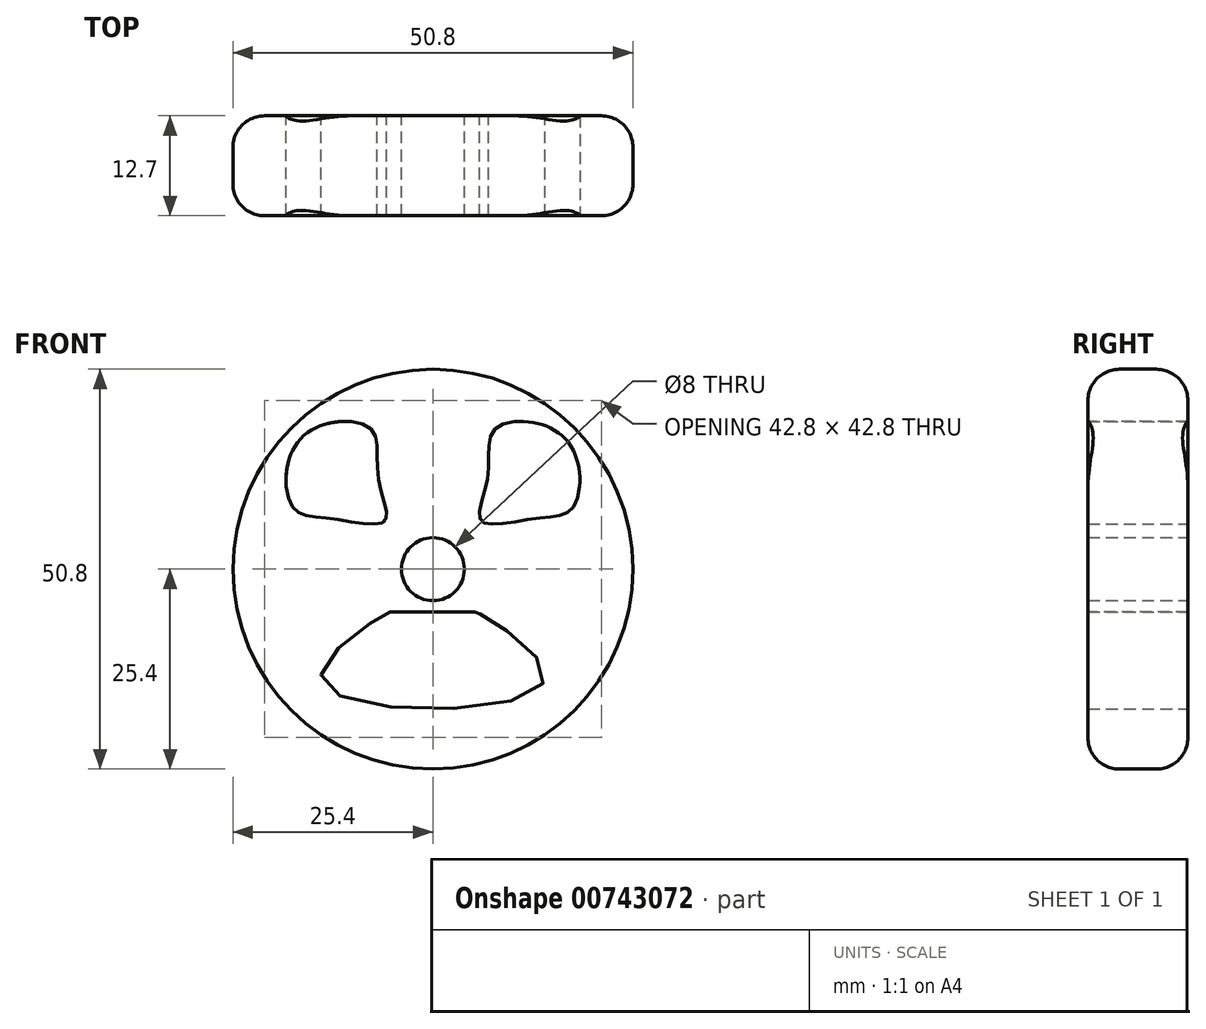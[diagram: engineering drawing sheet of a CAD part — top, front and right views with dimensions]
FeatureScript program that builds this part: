
annotation { "Feature Type Name" : "Feature", "Feature Type Description" : "" }
export const myFeature = defineFeature(function(context is Context, id is Id, definition is map)
    precondition{}
    {
        {
            var Q0;
            Q0=qCreatedBy(makeId("Front.planeOp"),FACE);
            var sketch = newSketch(context, id + "F0", { "sketchPlane" : qUnion([Q0])});
            skCircle(sketch, "E0", {"center": v(0, 0) * mm, "radius": 25.4 * mm});
            skCircle(sketch, "E1", {"center": v(0, 0) * mm, "radius": 4 * mm});
            skLineSegment(sketch, "E2", {"start": v(-17.96, 17.96) * mm, "end": v(0, 0) * mm, "construction": true});
            skLineSegment(sketch, "E3.MirrorCS", {"start": v(17.96, 17.96) * mm, "end": v(0, 0) * mm, "construction": true});
            skLineSegment(sketch, "E4", {"start": v(-14.15, -14.15) * mm, "end": v(14.15, -14.15) * mm, "construction": true});
            skLineSegment(sketch, "E5", {"start": v(-5.44, -5.44) * mm, "end": v(5.44, -5.44) * mm, "construction": true});
            skFitSpline(sketch, "E6", {"points": [v(-5.44, -5.44) * mm, v(-5.37, -5.44) * mm, v(-5.33, -5.44) * mm, v(-5.25, -5.44) * mm, v(-5.07, -5.44) * mm, v(-4.94, -5.44) * mm, v(-4.54, -5.44) * mm, v(-4.13, -5.44) * mm, v(-3.46, -5.44) * mm, v(-2.72, -5.44) * mm, v(0, -5.44) * mm, v(2.43, -5.44) * mm, v(3.14, -5.44) * mm, v(3.95, -5.44) * mm, v(4.25, -5.44) * mm, v(4.79, -5.44) * mm, v(4.98, -5.44) * mm, v(5.1, -5.44) * mm, v(5.2, -5.44) * mm, v(5.31, -5.44) * mm, v(5.36, -5.44) * mm, v(5.44, -5.44) * mm, v(14.15, -14.15) * mm, v(-14.15, -14.15) * mm, v(-5.44, -5.44) * mm]});
            skLineSegment(sketch, "E7", {"start": v(-12.92, 12.92) * mm, "end": v(-7.97, 17.87) * mm, "construction": true});
            skLineSegment(sketch, "E8.MirrorCS", {"start": v(-12.92, 12.92) * mm, "end": v(-17.87, 7.97) * mm, "construction": true});
            skFitSpline(sketch, "E9", {"points": [v(-17.87, 7.97) * mm, v(-16.7, 16.7) * mm, v(-7.97, 17.87) * mm, v(-6.98, 11.78) * mm, v(-6.13, 6.13) * mm, v(-13, 6.44) * mm, v(-17.87, 7.97) * mm]});
            skFitSpline(sketch, "E10.MirrorC", {"points": [v(17.87, 7.97) * mm, v(16.7, 16.7) * mm, v(7.97, 17.87) * mm, v(6.98, 11.78) * mm, v(6.13, 6.13) * mm, v(13, 6.44) * mm, v(17.87, 7.97) * mm]});
            skSolve(sketch);
        }
        {
            var Q0;
            Q0=qSketchRegion(id+"F0",true);
            extrude(context, id + "F1", {"entities" : qUnion([Q0]), "depth" : 12.7 * mm, "offsetDistance" : 25 * mm});
        }
        {
            var Q0;
            Q0=makeQuery(id+"F1.opExtrude","CAP_EDGE",EDGE,{"disambiguationData":[OSD([sQuery(id+"F0.wireOp",EDGE,"E0")])],"isStart":true});
            var Q1;
            Q1=makeQuery(id+"F1.opExtrude","CAP_EDGE",EDGE,{"disambiguationData":[OSD([sQuery(id+"F0.wireOp",EDGE,"E0")])],"isStart":false});
            fillet(context, id + "F2", {"entities" : qUnion([Q0, Q1]), "radius" : 4 * mm, "tangentPropagation" : true, "allowEdgeOverflow" : false});
        }
    });
